# Revit family: 202_PINODq-_
name_source: partatom
category: Air Terminals
units: mm (PartAtom-declared; Revit-internal decimal feet)

## family parameters
Always vertical = Yes
Cut with Voids When Loaded = No
Part Type = Normal
Room Calculation Point = Yes
Round Connector Dimension = Use Diameter
Shared = No
Work Plane-Based = No

## types (3) — shared parameters
CAT0 = Yes
CL_Location_5000 = 5000 mm  [stored 16.4042 ft]
Description = Extract valve
L_ARR = 400 mm  [stored 1.31234 ft]
Manufacturer = Climecon
QmdConnectorList = 201;D
URL = www.climecon.fi
W_ARR = 400 mm  [stored 1.31234 ft]
XRefLineVPlnId = 7453
YRefLineVPlnId = 7456
magiPartTypeId = 202
magiProductFamilyId = PINODq-*
zero-valued in all types: CLBTZ, H_ARR, MC_Default_elevation

## per-type parameters (varying)
| type | A | AA | BB | C1 | C2 | D |
| PINODq-100 | 150 mm  [stored 0.492126 ft] | 75 mm  [stored 0.246063 ft] | 82 mm  [stored 0.269029 ft] | 8 mm  [stored 0.0262467 ft] | 12 mm  [stored 0.0393701 ft] | 100 mm |
| PINODq-160 | 210 mm  [stored 0.688976 ft] | 105 mm  [stored 0.344488 ft] | 116 mm | 12 mm  [stored 0.0393701 ft] | 18 mm  [stored 0.0590551 ft] | 160 mm |
| PINODq-125 | 175 mm  [stored 0.574147 ft] | 88 mm | 96 mm  [stored 0.314961 ft] | 10 mm  [stored 0.0328084 ft] | 15 mm  [stored 0.0492126 ft] | 125 mm |

note: column(s) folded — value = type name in every type: magiProductCode, magiProductId

note: [stored X ft] marks values corroborated as IEEE doubles in the binary element streams (Revit-internal decimal feet)

## geometry (parser evidence)
native form markers: Sweep x2
no freeform markers — native parametric forms only
